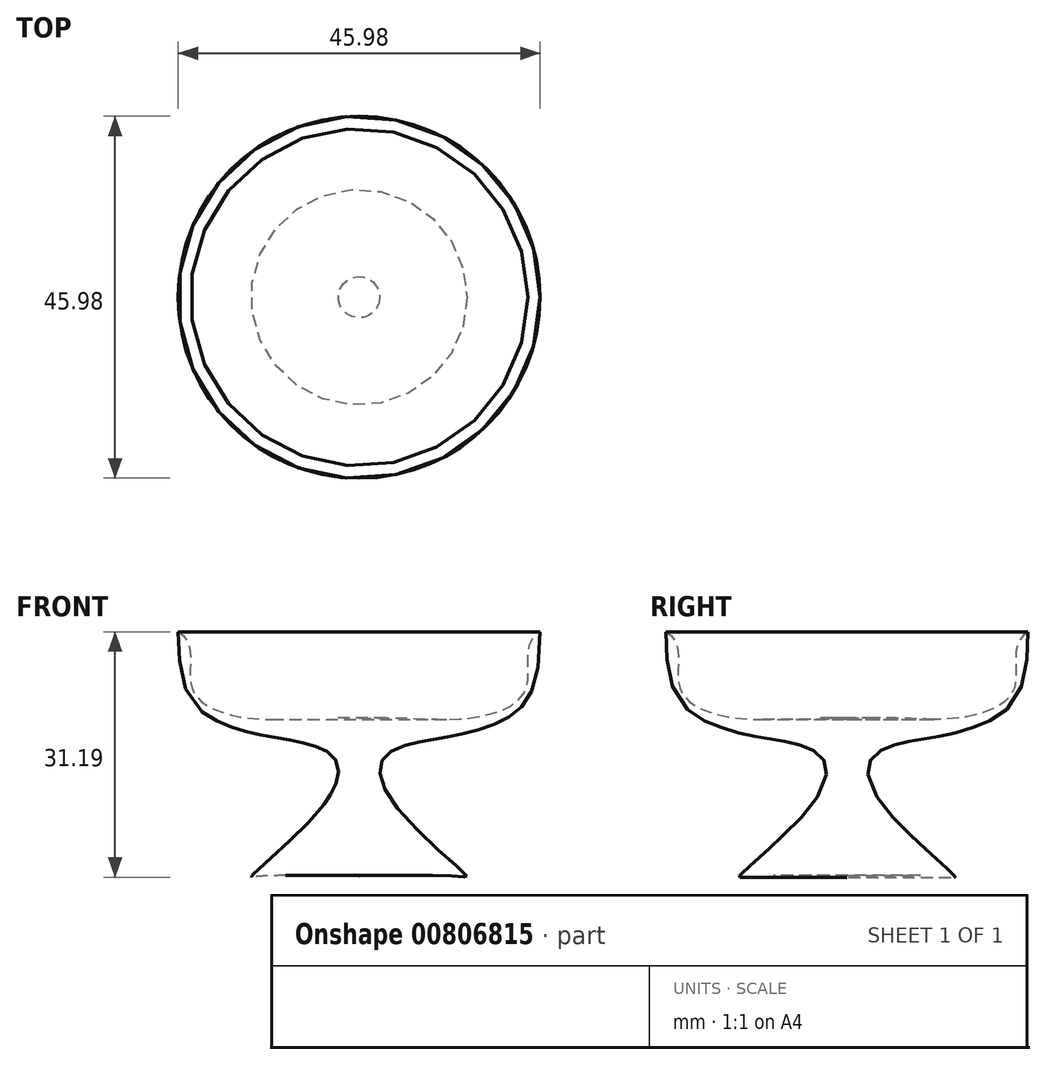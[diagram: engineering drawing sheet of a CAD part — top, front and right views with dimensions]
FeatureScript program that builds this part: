
annotation { "Feature Type Name" : "Feature", "Feature Type Description" : "" }
export const myFeature = defineFeature(function(context is Context, id is Id, definition is map)
    precondition{}
    {
        {
            var Q0;
            Q0=qCreatedBy(makeId("Front.planeOp"),FACE);
            var sketch = newSketch(context, id + "F0", { "sketchPlane" : qUnion([Q0])});
            skFitSpline(sketch, "E0", {"points": [v(22.99, 31.12) * mm, v(18.6, 20.05) * mm, v(12.37, 17.98) * mm, v(7.54, 17.1) * mm, v(3.09, 15) * mm, v(4.56, 9.06) * mm, v(13.7, 0) * mm, v(13.13, 0) * mm, v(0, 0) * mm], "startDerivative": vector(1.47, -137.13) * mm, "endDerivative": vector(-105.85, -1.92) * mm});
            skLineSegment(sketch, "E1", {"start": v(0, 31.43) * mm, "end": v(0, -5.04) * mm});
            skFitSpline(sketch, "E2", {"points": [v(0, 20.1) * mm, v(8.66, 20.05) * mm, v(14.73, 20.25) * mm, v(19.73, 22) * mm, v(21.36, 24.44) * mm, v(21.44, 28.19) * mm, v(22.99, 31.12) * mm], "startDerivative": vector(43.1, 2.6) * mm, "endDerivative": vector(25.55, 15.73) * mm});
            skSolve(sketch);
        }
        {
            var Q0;
            {var subQ0=sQuery(id+"F0.wireOp",EDGE,"E0");Q0=makeQuery(id+"F0.imprint","IMPRINT",FACE,{"disambiguationData":[TD([[makeQuery(id+"F0.imprint","IMPRINT",EDGE,{"derivedFrom":subQ0}),-1.0]])]});}
            var Q1;
            Q1=sQuery(id+"F0.wireOp",EDGE,"E1");
            revolve(context, id + "F1", {"surfaceOperationType" : NewSurfaceOperationType.NEW, "entities" : qUnion([Q0]), "axis" : qUnion([Q1]), "revolveType" : RevolveType.FULL});
        }
    });
